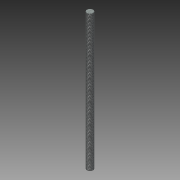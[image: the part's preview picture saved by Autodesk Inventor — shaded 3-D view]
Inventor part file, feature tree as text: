
AUTODESK INVENTOR PART (.ipt)
format: ipt  version: 2012 (Build 160160000, 160)  size: 68,096 bytes
history: native  units: mm
features: extrude x1, thread x1, sketch x1
ambient origin geometry x8: Origin, YZ Plane, XZ Plane, XY Plane, X Axis, Y Axis, Z Axis, Center Point
bodies: Solid1 (feature_tree)
feature tree (3):
  extrude  "Extrusion1"  Depth=179.5mm TaperAngle=0.0deg
  thread  "Thread1"  [1 undecoded]
  sketch  "Sketch1"  dims[d0=8.0mm d1=179.5mm d2=0.0mm d3=10.0mm d4=0.0mm]
note: 1 required parameter value undecoded (feature->parameter linkage not recoverable at this tier; creation-order binding heuristic only, values carry confidence <= 0.55)
